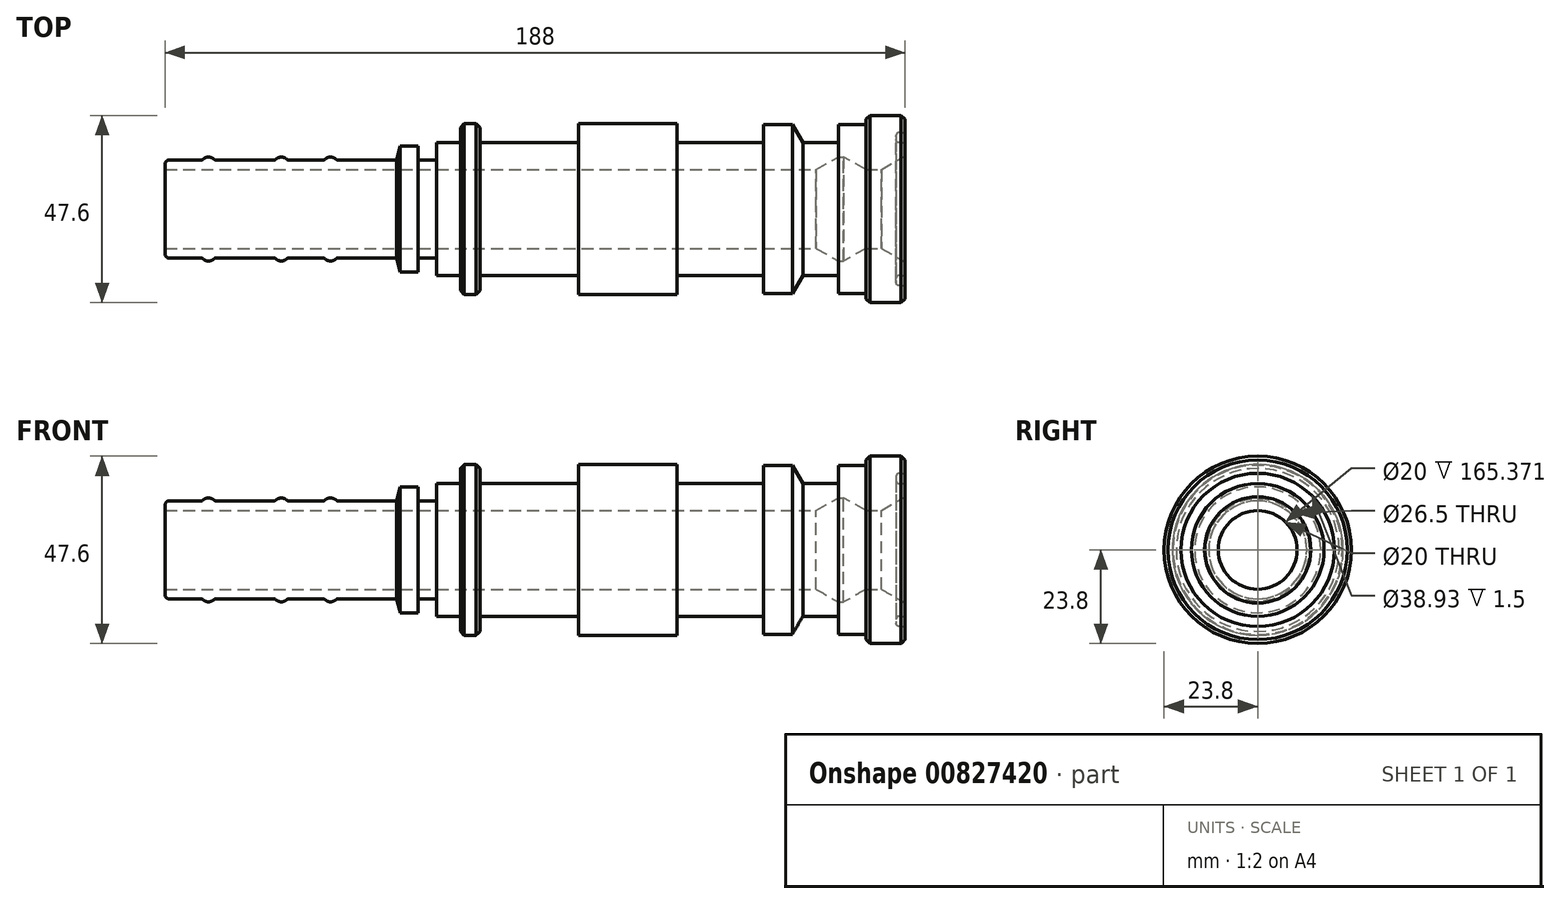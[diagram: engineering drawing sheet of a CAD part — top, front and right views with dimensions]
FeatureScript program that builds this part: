
annotation { "Feature Type Name" : "Feature", "Feature Type Description" : "" }
export const myFeature = defineFeature(function(context is Context, id is Id, definition is map)
    precondition{}
    {
        {
            var Q0;
            Q0=qCreatedBy(makeId("Front.planeOp"),FACE);
            var sketch = newSketch(context, id + "F0", { "sketchPlane" : qUnion([Q0])});
            skLineSegment(sketch, "E0", {"start": v(0, 23.8) * mm, "end": v(-10, 23.8) * mm});
            skLineSegment(sketch, "E1", {"start": v(-10, 23.8) * mm, "end": v(-10, 21.5) * mm});
            skLineSegment(sketch, "E2", {"start": v(-10, 21.5) * mm, "end": v(-17, 21.5) * mm});
            skLineSegment(sketch, "E3", {"start": v(-17, 21.5) * mm, "end": v(-17, 16.85) * mm});
            skLineSegment(sketch, "E4", {"start": v(-17, 16.85) * mm, "end": v(-26, 16.85) * mm});
            skLineSegment(sketch, "E5", {"start": v(-26, 16.85) * mm, "end": v(-28.68, 21.5) * mm});
            skLineSegment(sketch, "E6", {"start": v(-28.68, 21.5) * mm, "end": v(-36, 21.5) * mm});
            skLineSegment(sketch, "E7", {"start": v(-36, 21.5) * mm, "end": v(-36, 16.85) * mm});
            skLineSegment(sketch, "E8", {"start": v(-36, 16.85) * mm, "end": v(-58, 16.85) * mm});
            skLineSegment(sketch, "E9", {"start": v(-58, 16.85) * mm, "end": v(-58, 21.7) * mm});
            skLineSegment(sketch, "E10", {"start": v(-58, 21.7) * mm, "end": v(-83, 21.7) * mm});
            skLineSegment(sketch, "E11", {"start": v(-83, 21.7) * mm, "end": v(-83, 16.85) * mm});
            skLineSegment(sketch, "E12", {"start": v(-83, 16.85) * mm, "end": v(-108, 16.85) * mm});
            skLineSegment(sketch, "E13", {"start": v(-108, 16.85) * mm, "end": v(-108, 21.7) * mm});
            skLineSegment(sketch, "E14", {"start": v(-108, 21.7) * mm, "end": v(-113, 21.7) * mm});
            skLineSegment(sketch, "E15", {"start": v(-113, 21.7) * mm, "end": v(-113, 16.85) * mm});
            skLineSegment(sketch, "E16", {"start": v(-113, 16.85) * mm, "end": v(-119, 16.85) * mm});
            skLineSegment(sketch, "E17", {"start": v(-119, 16.85) * mm, "end": v(-119, 12.45) * mm});
            skLineSegment(sketch, "E18", {"start": v(-119, 12.45) * mm, "end": v(-123.8, 12.45) * mm});
            skLineSegment(sketch, "E19", {"start": v(-123.8, 12.45) * mm, "end": v(-123.8, 16) * mm});
            skLineSegment(sketch, "E20", {"start": v(-123.8, 16) * mm, "end": v(-128.3, 16) * mm});
            skLineSegment(sketch, "E21", {"start": v(-128.3, 16) * mm, "end": v(-129.25, 12.45) * mm});
            skLineSegment(sketch, "E22", {"start": v(-178.56, 12.45) * mm, "end": v(-188, 12.45) * mm});
            skLineSegment(sketch, "E23", {"start": v(-188, 12.45) * mm, "end": v(-188, 10) * mm});
            skLineSegment(sketch, "E24", {"start": v(-188, 10) * mm, "end": v(-22.63, 10) * mm});
            skLineSegment(sketch, "E25", {"start": v(0, 13.49) * mm, "end": v(0, 16.85) * mm});
            skLineSegment(sketch, "E26", {"start": v(0, 0) * mm, "end": v(-236.28, 0) * mm, "construction": true});
            skLineSegment(sketch, "E27", {"start": v(-184.07, 13.2) * mm, "end": v(-136.58, 13.2) * mm, "construction": true});
            skArc(sketch, "E28", {"start": v(-175.44, 12.45) * mm, "mid": v(-177, 13.2) * mm, "end": v(-178.56, 12.45) * mm});
            skPoint(sketch, "E29.orphan", {"position": v(-177, 12.45) * mm});
            skLineSegment(sketch, "E30", {"start": v(-175.44, 12.45) * mm, "end": v(-160.06, 12.45) * mm});
            skArc(sketch, "E31", {"start": v(-156.94, 12.45) * mm, "mid": v(-158.5, 13.2) * mm, "end": v(-160.06, 12.45) * mm});
            skArc(sketch, "E32", {"start": v(-144.44, 12.45) * mm, "mid": v(-146, 13.2) * mm, "end": v(-147.56, 12.45) * mm});
            skLineSegment(sketch, "E33", {"start": v(-156.94, 12.45) * mm, "end": v(-147.56, 12.45) * mm});
            skLineSegment(sketch, "E34", {"start": v(-144.44, 12.45) * mm, "end": v(-129.25, 12.45) * mm});
            skLineSegment(sketch, "E35", {"start": v(0, 19.47) * mm, "end": v(-2.3, 19.47) * mm});
            skLineSegment(sketch, "E36", {"start": v(-2.3, 19.47) * mm, "end": v(-2.3, 16.85) * mm});
            skLineSegment(sketch, "E37", {"start": v(-2.3, 16.85) * mm, "end": v(0, 16.85) * mm});
            skLineSegment(sketch, "E38.trimOffspring", {"start": v(0, 19.47) * mm, "end": v(0, 23.8) * mm});
            skLineSegment(sketch, "E39", {"start": v(0, 13.49) * mm, "end": v(-6.04, 10) * mm});
            skLineSegment(sketch, "E40", {"start": v(-10, 10) * mm, "end": v(-15.63, 13.25) * mm});
            skLineSegment(sketch, "E41", {"start": v(-15.63, 13.25) * mm, "end": v(-17, 13.25) * mm});
            skLineSegment(sketch, "E42", {"start": v(-17, 13.25) * mm, "end": v(-22.63, 10) * mm});
            skLineSegment(sketch, "E43.trimOffspring", {"start": v(-10, 10) * mm, "end": v(-6.04, 10) * mm});
            skPoint(sketch, "E44.orphan", {"position": v(0, 10) * mm});
            skSolve(sketch);
        }
        {
            var Q0;
            Q0=makeQuery(id+"F0.imprint","IMPRINT",FACE,{"disambiguationData":[TD([[makeQuery(id+"F0.imprint","IMPRINT",EDGE,{"derivedFrom":sQuery(id+"F0.wireOp",EDGE,"E0")}),1.0]])]});
            var Q1;
            Q1=sQuery(id+"F0.wireOp",EDGE,"E26");
            revolve(context, id + "F1", {"surfaceOperationType" : NewSurfaceOperationType.NEW, "entities" : qUnion([Q0]), "axis" : qUnion([Q1]), "revolveType" : RevolveType.FULL});
        }
        {
            var Q0;
            Q0=makeQuery(id+"F1.opRevolve","SWEPT_EDGE",EDGE,{"disambiguationData":[OSD([sQuery(id+"F0.wireOp",EDGE,"E13"),sQuery(id+"F0.wireOp",EDGE,"E14")])]});
            var Q1;
            Q1=makeQuery(id+"F1.opRevolve","SWEPT_EDGE",EDGE,{"disambiguationData":[OSD([sQuery(id+"F0.wireOp",EDGE,"E14"),sQuery(id+"F0.wireOp",EDGE,"E15")])]});
            var Q2;
            Q2=makeQuery(id+"F1.opRevolve","SWEPT_EDGE",EDGE,{"disambiguationData":[OSD([sQuery(id+"F0.wireOp",EDGE,"E0"),sQuery(id+"F0.wireOp",EDGE,"E38.trimOffspring")])]});
            var Q3;
            Q3=makeQuery(id+"F1.opRevolve","SWEPT_EDGE",EDGE,{"disambiguationData":[OSD([sQuery(id+"F0.wireOp",EDGE,"E0"),sQuery(id+"F0.wireOp",EDGE,"E1")])]});
            chamfer(context, id + "F2", {"entities" : qUnion([Q0, Q1, Q2, Q3]), "width" : 1 * mm, "tangentPropagation" : true});
        }
        {
            var Q0;
            Q0=makeQuery(id+"F1.opRevolve","SWEPT_EDGE",EDGE,{"disambiguationData":[OSD([sQuery(id+"F0.wireOp",EDGE,"E28"),sQuery(id+"F0.wireOp",EDGE,"E30")])]});
            var Q1;
            Q1=makeQuery(id+"F1.opRevolve","SWEPT_EDGE",EDGE,{"disambiguationData":[OSD([sQuery(id+"F0.wireOp",EDGE,"E31"),sQuery(id+"F0.wireOp",EDGE,"E33")])]});
            var Q2;
            Q2=makeQuery(id+"F1.opRevolve","SWEPT_EDGE",EDGE,{"disambiguationData":[OSD([sQuery(id+"F0.wireOp",EDGE,"E32"),sQuery(id+"F0.wireOp",EDGE,"E34")])]});
            var Q3;
            Q3=makeQuery(id+"F1.opRevolve","SWEPT_EDGE",EDGE,{"disambiguationData":[OSD([sQuery(id+"F0.wireOp",EDGE,"E32"),sQuery(id+"F0.wireOp",EDGE,"E33")])]});
            var Q4;
            Q4=makeQuery(id+"F1.opRevolve","SWEPT_EDGE",EDGE,{"disambiguationData":[OSD([sQuery(id+"F0.wireOp",EDGE,"E30"),sQuery(id+"F0.wireOp",EDGE,"E31")])]});
            var Q5;
            Q5=makeQuery(id+"F1.opRevolve","SWEPT_EDGE",EDGE,{"disambiguationData":[OSD([sQuery(id+"F0.wireOp",EDGE,"E22"),sQuery(id+"F0.wireOp",EDGE,"E28")])]});
            fillet(context, id + "F3", {"entities" : qUnion([Q0, Q1, Q2, Q3, Q4, Q5]), "radius" : .8 * mm, "tangentPropagation" : true, "allowEdgeOverflow" : false});
        }
        {
            var Q0;
            Q0=makeQuery(id+"F1.opRevolve","SWEPT_EDGE",EDGE,{"disambiguationData":[OSD([sQuery(id+"F0.wireOp",EDGE,"E22"),sQuery(id+"F0.wireOp",EDGE,"E23")])]});
            fillet(context, id + "F4", {"entities" : qUnion([Q0]), "radius" : 1 * mm, "tangentPropagation" : true, "allowEdgeOverflow" : false});
        }
        {
            var Q0;
            Q0=makeQuery(id+"F1.opRevolve","SWEPT_EDGE",EDGE,{"disambiguationData":[OSD([sQuery(id+"F0.wireOp",EDGE,"E17"),sQuery(id+"F0.wireOp",EDGE,"E18")])]});
            var Q1;
            Q1=makeQuery(id+"F1.opRevolve","SWEPT_EDGE",EDGE,{"disambiguationData":[OSD([sQuery(id+"F0.wireOp",EDGE,"E18"),sQuery(id+"F0.wireOp",EDGE,"E19")])]});
            fillet(context, id + "F5", {"entities" : qUnion([Q0, Q1]), "radius" : .4 * mm, "tangentPropagation" : true, "allowEdgeOverflow" : false});
        }
        {
            var Q0;
            Q0=makeQuery(id+"F1.opRevolve","SWEPT_EDGE",EDGE,{"disambiguationData":[OSD([sQuery(id+"F0.wireOp",EDGE,"E11"),sQuery(id+"F0.wireOp",EDGE,"E12")])]});
            var Q1;
            Q1=makeQuery(id+"F1.opRevolve","SWEPT_EDGE",EDGE,{"disambiguationData":[OSD([sQuery(id+"F0.wireOp",EDGE,"E7"),sQuery(id+"F0.wireOp",EDGE,"E8")])]});
            var Q2;
            Q2=makeQuery(id+"F1.opRevolve","SWEPT_EDGE",EDGE,{"disambiguationData":[OSD([sQuery(id+"F0.wireOp",EDGE,"E8"),sQuery(id+"F0.wireOp",EDGE,"E9")])]});
            var Q3;
            Q3=makeQuery(id+"F1.opRevolve","SWEPT_EDGE",EDGE,{"disambiguationData":[OSD([sQuery(id+"F0.wireOp",EDGE,"E12"),sQuery(id+"F0.wireOp",EDGE,"E13")])]});
            fillet(context, id + "F6", {"entities" : qUnion([Q0, Q1, Q2, Q3]), "radius" : .5 * mm, "tangentPropagation" : true, "allowEdgeOverflow" : false});
        }
        {
            var Q0;
            Q0=makeQuery(id+"F1.opRevolve","SWEPT_EDGE",EDGE,{"disambiguationData":[OSD([sQuery(id+"F0.wireOp",EDGE,"E35"),sQuery(id+"F0.wireOp",EDGE,"E36")])]});
            var Q1;
            Q1=makeQuery(id+"F1.opRevolve","SWEPT_EDGE",EDGE,{"disambiguationData":[OSD([sQuery(id+"F0.wireOp",EDGE,"E36"),sQuery(id+"F0.wireOp",EDGE,"E37")])]});
            fillet(context, id + "F7", {"entities" : qUnion([Q0, Q1]), "radius" : .8 * mm, "tangentPropagation" : true, "allowEdgeOverflow" : false});
        }
    });
